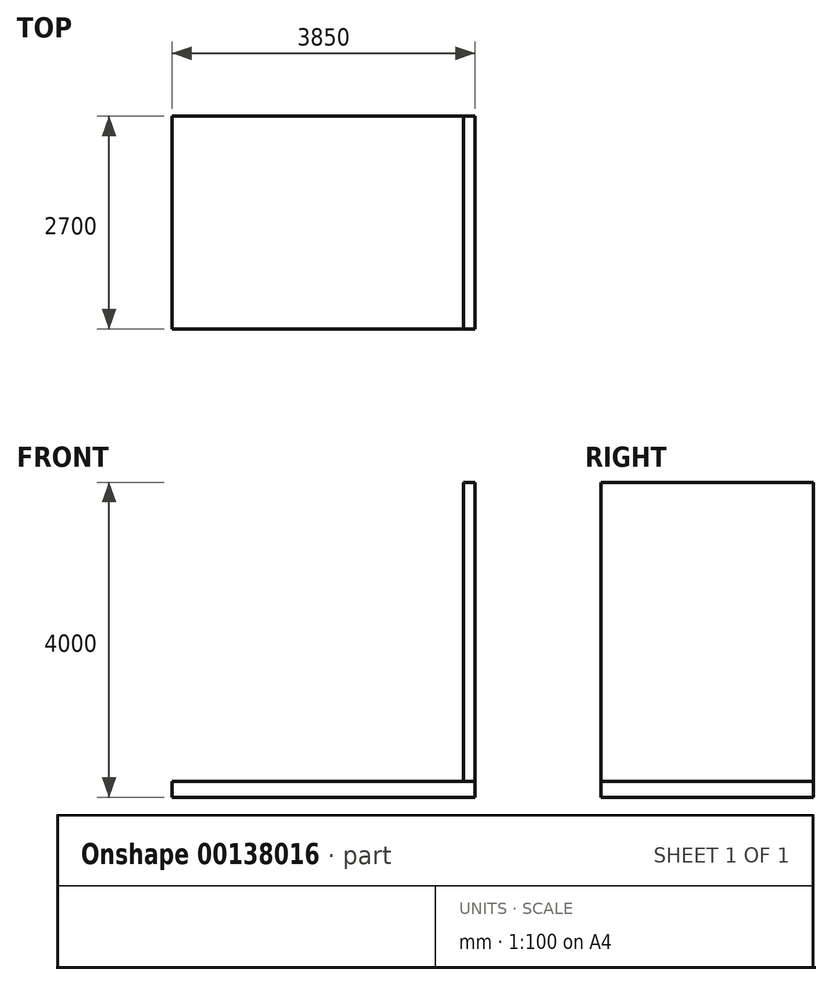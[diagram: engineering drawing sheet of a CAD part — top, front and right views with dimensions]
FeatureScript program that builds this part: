
annotation { "Feature Type Name" : "Feature", "Feature Type Description" : "" }
export const myFeature = defineFeature(function(context is Context, id is Id, definition is map)
    precondition{}
    {
        {
            var Q0;
            Q0=qCreatedBy(makeId("Top.planeOp"),FACE);
            var sketch = newSketch(context, id + "F0", { "sketchPlane" : qUnion([Q0])});
            skLineSegment(sketch, "E0.bottom", {"start": v(1925, -1350) * mm, "end": v(-1925, -1350) * mm});
            skLineSegment(sketch, "E0.top", {"start": v(1925, 1350) * mm, "end": v(-1925, 1350) * mm});
            skLineSegment(sketch, "E0.left", {"start": v(1925, -1350) * mm, "end": v(1925, 1350) * mm});
            skLineSegment(sketch, "E0.right", {"start": v(-1925, -1350) * mm, "end": v(-1925, 1350) * mm});
            skPoint(sketch, "E0.middle", {"position": v(0, 0) * mm});
            skSolve(sketch);
        }
        {
            var Q0;
            Q0=makeQuery(id+"F0.imprint","IMPRINT",FACE,{"disambiguationData":[TD([[makeQuery(id+"F0.imprint","IMPRINT",EDGE,{"derivedFrom":sQuery(id+"F0.wireOp",EDGE,"E0.bottom")}),-1.0]])]});
            extrude(context, id + "F1", {"entities" : qUnion([Q0]), "depth" : 200 * mm});
        }
        {
            var Q0;
            Q0=makeQuery(id+"F1.opExtrude","CAP_FACE",FACE,{"disambiguationData":[OSD([sQuery(id+"F0.wireOp",EDGE,"E0.bottom"),sQuery(id+"F0.wireOp",EDGE,"E0.top"),sQuery(id+"F0.wireOp",EDGE,"E0.left"),sQuery(id+"F0.wireOp",EDGE,"E0.right")])],"isStart":false});
            var sketch = newSketch(context, id + "F2", { "sketchPlane" : qUnion([Q0])});
            skLineSegment(sketch, "E1.bottom", {"start": v(-1925, -1350) * mm, "end": v(-1775, -1350) * mm});
            skLineSegment(sketch, "E1.top", {"start": v(-1925, 1350) * mm, "end": v(-1775, 1350) * mm});
            skLineSegment(sketch, "E1.left", {"start": v(-1925, -1350) * mm, "end": v(-1925, 1350) * mm});
            skLineSegment(sketch, "E1.right", {"start": v(-1775, -1350) * mm, "end": v(-1775, 1350) * mm});
            skLineSegment(sketch, "E2.bottom", {"start": v(1925, -1350) * mm, "end": v(1775, -1350) * mm});
            skLineSegment(sketch, "E2.top", {"start": v(1925, 1350) * mm, "end": v(1775, 1350) * mm});
            skLineSegment(sketch, "E2.left", {"start": v(1925, -1350) * mm, "end": v(1925, 1350) * mm});
            skLineSegment(sketch, "E2.right", {"start": v(1775, -1350) * mm, "end": v(1775, 1350) * mm});
            skLineSegment(sketch, "E3.bottom", {"start": v(-1775, 1350) * mm, "end": v(1775, 1350) * mm});
            skLineSegment(sketch, "E3.top", {"start": v(-1775, 1150) * mm, "end": v(1775, 1150) * mm});
            skLineSegment(sketch, "E3.left", {"start": v(-1775, 1350) * mm, "end": v(-1775, 1150) * mm});
            skLineSegment(sketch, "E3.right", {"start": v(1775, 1350) * mm, "end": v(1775, 1150) * mm});
            skSolve(sketch);
        }
        {
            var Q0;
            Q0=makeQuery(id+"F2.imprint","IMPRINT",FACE,{"disambiguationData":[TD([[makeQuery(id+"F2.imprint","IMPRINT",EDGE,{"derivedFrom":sQuery(id+"F2.wireOp",EDGE,"E2.bottom")}),-1.0]])]});
            extrude(context, id + "F3", {"entities" : qUnion([Q0]), "depth" : 3800 * mm});
        }
    });
